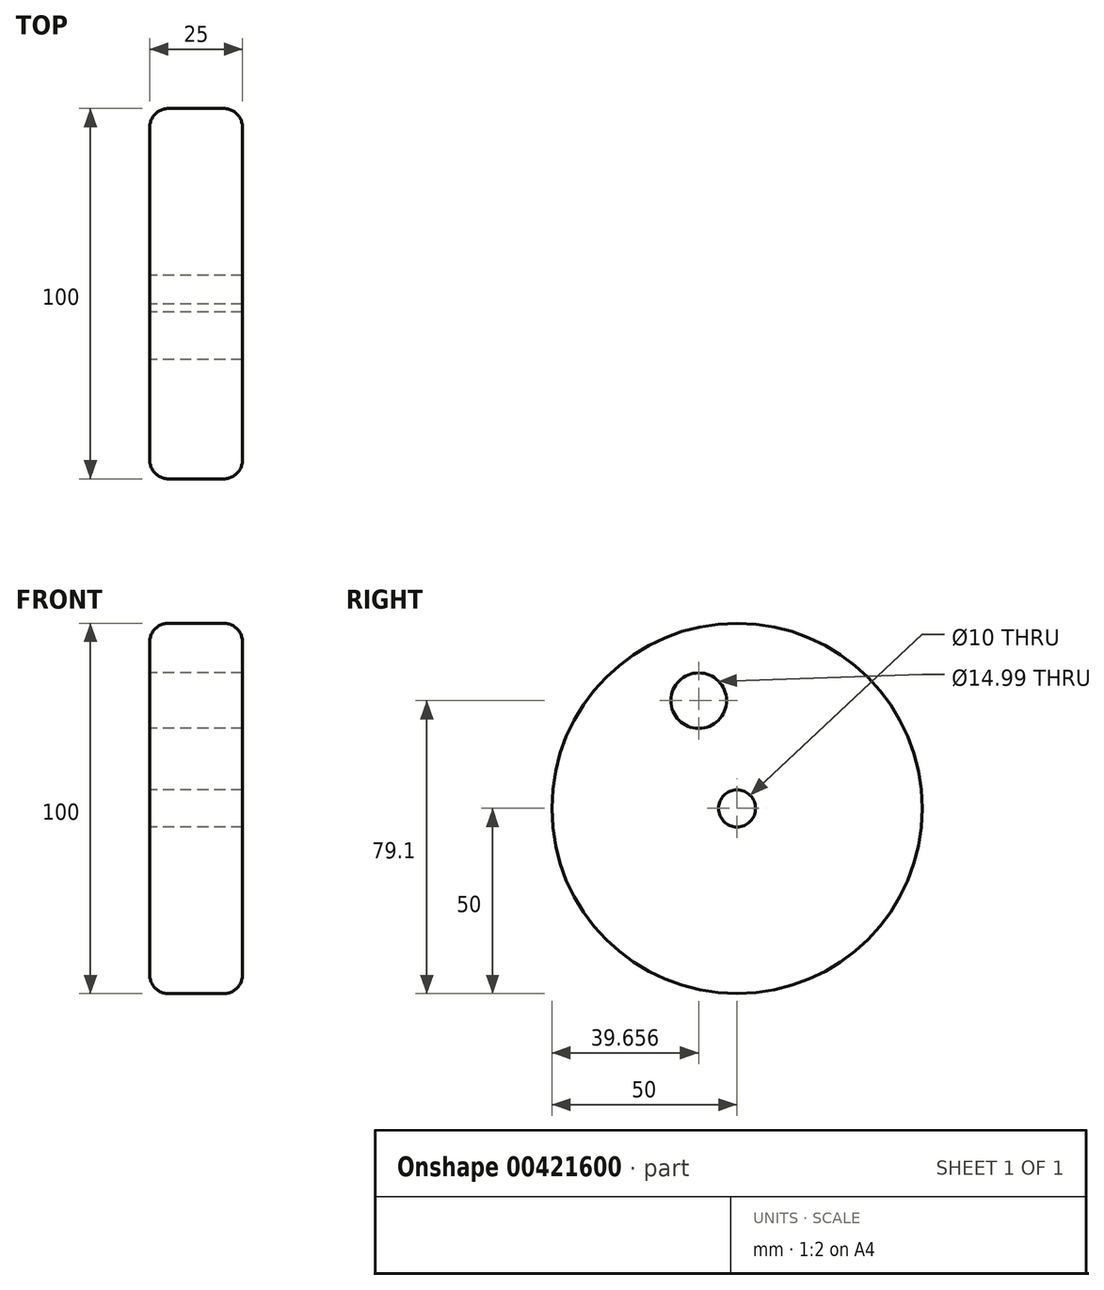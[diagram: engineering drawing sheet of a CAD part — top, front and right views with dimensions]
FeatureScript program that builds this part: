
annotation { "Feature Type Name" : "Feature", "Feature Type Description" : "" }
export const myFeature = defineFeature(function(context is Context, id is Id, definition is map)
    precondition{}
    {
        {
            var Q0;
            Q0=qCreatedBy(makeId("Right.planeOp"),FACE);
            var sketch = newSketch(context, id + "F0", { "sketchPlane" : qUnion([Q0])});
            skCircle(sketch, "E0", {"center": v(0, 0) * mm, "radius": 50 * mm});
            skCircle(sketch, "E1", {"center": v(0, 0) * mm, "radius": 5 * mm});
            skCircle(sketch, "E2", {"center": v(-10.34, 29.1) * mm, "radius": 7.5 * mm});
            skSolve(sketch);
        }
        {
            var Q0;
            Q0=makeQuery(id+"F0.imprint","IMPRINT",FACE,{"disambiguationData":[TD([[makeQuery(id+"F0.imprint","IMPRINT",EDGE,{"derivedFrom":sQuery(id+"F0.wireOp",EDGE,"E0")}),1.0]])]});
            extrude(context, id + "F1", {"entities" : qUnion([Q0]), "depth" : 25 * mm});
        }
        {
            var Q0;
            Q0=makeQuery(id+"F1.opExtrude","CAP_EDGE",EDGE,{"disambiguationData":[OSD([sQuery(id+"F0.wireOp",EDGE,"E0")])],"isStart":false});
            var Q1;
            Q1=makeQuery(id+"F1.opExtrude","CAP_EDGE",EDGE,{"disambiguationData":[OSD([sQuery(id+"F0.wireOp",EDGE,"E0")])],"isStart":true});
            fillet(context, id + "F2", {"entities" : qUnion([Q0, Q1]), "radius" : 5 * mm, "tangentPropagation" : true, "allowEdgeOverflow" : false});
        }
    });
